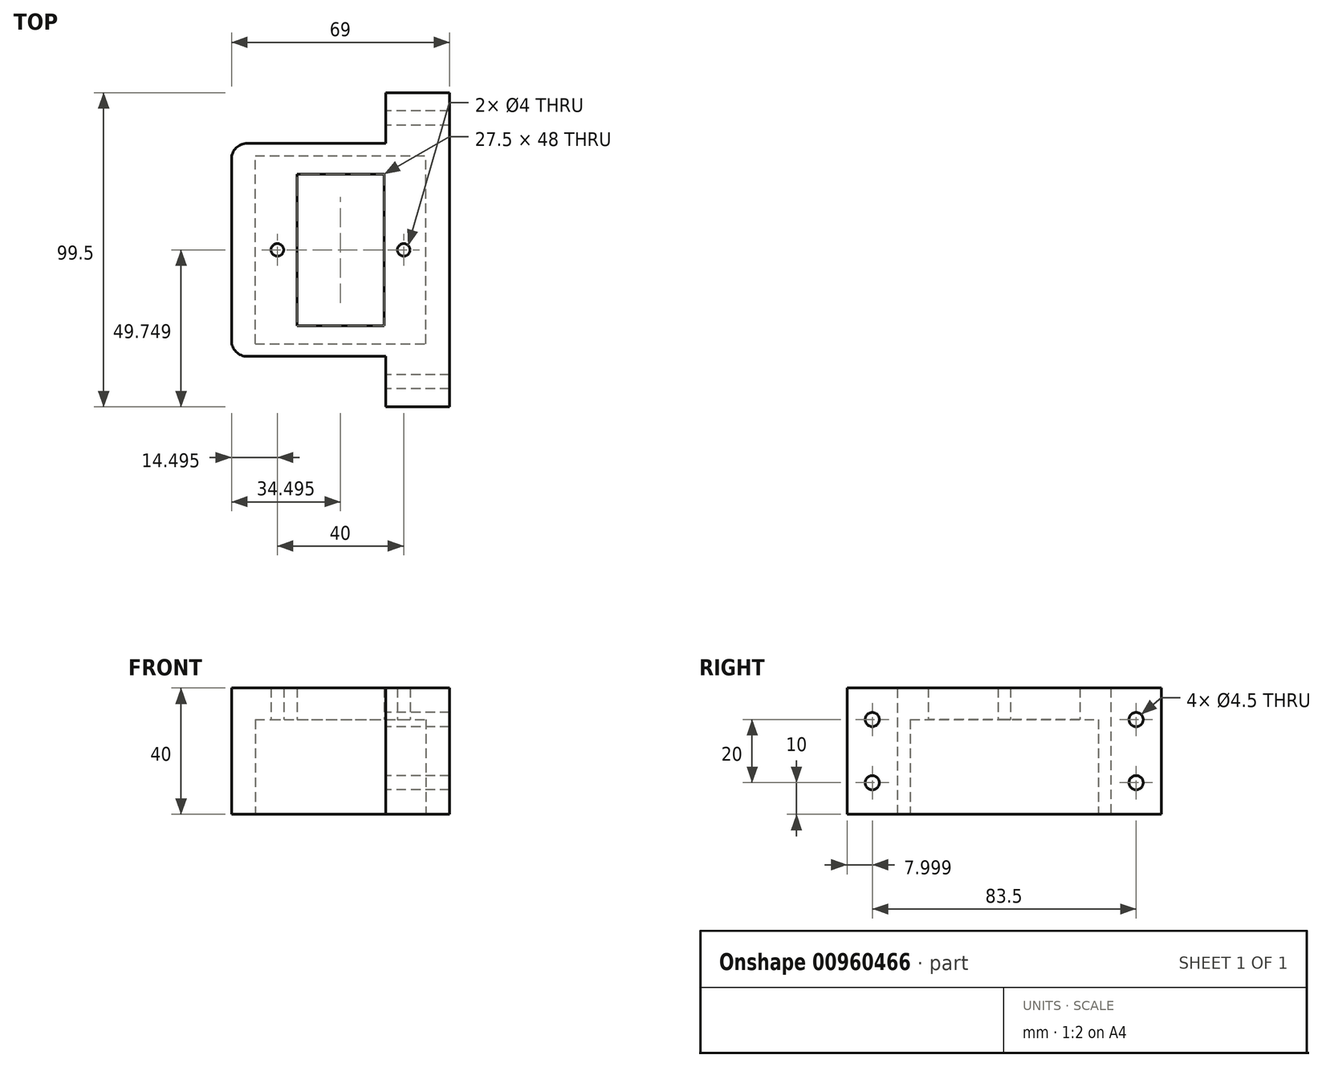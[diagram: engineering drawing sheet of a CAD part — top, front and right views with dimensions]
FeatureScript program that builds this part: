
annotation { "Feature Type Name" : "Feature", "Feature Type Description" : "" }
export const myFeature = defineFeature(function(context is Context, id is Id, definition is map)
    precondition{}
    {
        {
            var Q0;
            Q0=qCreatedBy(makeId("Top.planeOp"),FACE);
            var sketch = newSketch(context, id + "F0", { "sketchPlane" : qUnion([Q0])});
            skLineSegment(sketch, "E0.bottom", {"start": v(-20.47, 12.83) * mm, "end": v(7.03, 12.83) * mm});
            skLineSegment(sketch, "E0.top", {"start": v(-20.47, -35.17) * mm, "end": v(7.03, -35.17) * mm});
            skLineSegment(sketch, "E0.left", {"start": v(-20.47, 12.83) * mm, "end": v(-20.47, -35.17) * mm});
            skLineSegment(sketch, "E0.right", {"start": v(7.03, 12.83) * mm, "end": v(7.03, -35.17) * mm});
            skLineSegment(sketch, "E1", {"start": v(-20.47, -11.17) * mm, "end": v(-98.82, -11.17) * mm, "construction": true});
            skLineSegment(sketch, "E2", {"start": v(7.03, -11.17) * mm, "end": v(89.84, -11.17) * mm, "construction": true});
            skCircle(sketch, "E3", {"center": v(-26.72, -11.17) * mm, "radius": 2 * mm});
            skCircle(sketch, "E4", {"center": v(13.28, -11.17) * mm, "radius": 2 * mm});
            skLineSegment(sketch, "E5", {"start": v(-6.72, -35.17) * mm, "end": v(-6.72, 12.83) * mm, "construction": true});
            skLineSegment(sketch, "E6.bottom", {"start": v(-41.22, 38.58) * mm, "end": v(27.78, 38.58) * mm});
            skLineSegment(sketch, "E6.top", {"start": v(-41.22, -60.92) * mm, "end": v(27.78, -60.92) * mm});
            skLineSegment(sketch, "E6.left", {"start": v(-41.22, 38.58) * mm, "end": v(-41.22, -60.92) * mm});
            skLineSegment(sketch, "E6.right", {"start": v(27.78, 38.58) * mm, "end": v(27.78, -60.92) * mm});
            skLineSegment(sketch, "E7", {"start": v(-21.02, 18.58) * mm, "end": v(7.58, 18.58) * mm});
            skLineSegment(sketch, "E8", {"start": v(-20.47, -11.17) * mm, "end": v(7.03, -11.17) * mm, "construction": true});
            skLineSegment(sketch, "E9", {"start": v(-21.02, -40.92) * mm, "end": v(7.58, -40.92) * mm});
            skPoint(sketch, "E10", {"position": v(-31.22, -11.17) * mm});
            skPoint(sketch, "E11", {"position": v(17.78, -11.17) * mm});
            skLineSegment(sketch, "E12", {"start": v(-31.22, -11.17) * mm, "end": v(-21.02, 18.58) * mm});
            skLineSegment(sketch, "E13", {"start": v(7.58, 18.58) * mm, "end": v(17.78, -11.17) * mm});
            skLineSegment(sketch, "E14", {"start": v(17.78, -11.17) * mm, "end": v(7.58, -40.92) * mm});
            skLineSegment(sketch, "E15", {"start": v(-21.02, -40.92) * mm, "end": v(-31.22, -11.17) * mm});
            skSolve(sketch);
        }
        {
            var Q0;
            Q0=makeQuery(id+"F0.imprint","IMPRINT",FACE,{"disambiguationData":[TD([[makeQuery(id+"F0.imprint","IMPRINT",EDGE,{"derivedFrom":sQuery(id+"F0.wireOp",EDGE,"E0.bottom")}),1.0]])]});
            extrude(context, id + "F1", {"entities" : qUnion([Q0]), "depth" : 1 * mm, "offsetDistance" : 25 * mm});
        }
        {
            var Q0;
            Q0=makeQuery(id+"F0.imprint","IMPRINT",FACE,{"disambiguationData":[TD([[makeQuery(id+"F0.imprint","IMPRINT",EDGE,{"derivedFrom":sQuery(id+"F0.wireOp",EDGE,"E6.bottom")}),-1.0]])]});
            var Q1;
            Q1=makeQuery(id+"F0.imprint","IMPRINT",FACE,{"disambiguationData":[TD([[makeQuery(id+"F0.imprint","IMPRINT",EDGE,{"derivedFrom":sQuery(id+"F0.wireOp",EDGE,"E0.bottom")}),1.0]])]});
            extrude(context, id + "F2", {"entities" : qUnion([Q0, Q1]), "operationType" : NewBodyOperationType.ADD, "oppositeDirection" : true, "depth" : 40 * mm, "offsetDistance" : 25 * mm});
        }
        {
            var Q0;
            Q0=makeQuery(id+"F2.opExtrude","CAP_FACE",FACE,{"disambiguationData":[OSD([sQuery(id+"F0.wireOp",EDGE,"E0.bottom"),sQuery(id+"F0.wireOp",EDGE,"E0.top"),sQuery(id+"F0.wireOp",EDGE,"E0.left"),sQuery(id+"F0.wireOp",EDGE,"E0.right"),sQuery(id+"F0.wireOp",EDGE,"E3"),sQuery(id+"F0.wireOp",EDGE,"E4"),sQuery(id+"F0.wireOp",EDGE,"E6.bottom"),sQuery(id+"F0.wireOp",EDGE,"E6.top"),sQuery(id+"F0.wireOp",EDGE,"E6.left"),sQuery(id+"F0.wireOp",EDGE,"E6.right")])],"isStart":false});
            var sketch = newSketch(context, id + "F3", { "sketchPlane" : qUnion([Q0])});
            skLineSegment(sketch, "E16.bottom", {"start": v(-33.72, 40.92) * mm, "end": v(20.28, 40.92) * mm});
            skLineSegment(sketch, "E16.top", {"start": v(-33.72, -18.58) * mm, "end": v(20.28, -18.58) * mm});
            skLineSegment(sketch, "E16.left", {"start": v(-33.72, 40.92) * mm, "end": v(-33.72, -18.58) * mm});
            skLineSegment(sketch, "E16.right", {"start": v(20.28, 40.92) * mm, "end": v(20.28, -18.58) * mm});
            skSolve(sketch);
        }
        {
            var Q0;
            Q0=makeQuery(id+"F3.imprint","IMPRINT",FACE,{"disambiguationData":[TD([[makeQuery(id+"F3.imprint","IMPRINT",EDGE,{"derivedFrom":sQuery(id+"F3.wireOp",EDGE,"E16.bottom")}),-1.0]])]});
            var Q1;
            Q1=makeQuery(id+"F3.imprint","IMPRINT",FACE,{"disambiguationData":[TD([[makeQuery(id+"F3.imprint","IMPRINT",EDGE,{"derivedFrom":makeQuery(id+"F2.opExtrude","CAP_EDGE",EDGE,{"disambiguationData":[OSD([sQuery(id+"F0.wireOp",EDGE,"E3")])],"isStart":false})}),-1.0]])]});
            var Q2;
            Q2=makeQuery(id+"F3.imprint","IMPRINT",FACE,{"disambiguationData":[TD([[makeQuery(id+"F3.imprint","IMPRINT",EDGE,{"derivedFrom":makeQuery(id+"F2.opExtrude","CAP_EDGE",EDGE,{"disambiguationData":[OSD([sQuery(id+"F0.wireOp",EDGE,"E4")])],"isStart":false})}),-1.0]])]});
            extrude(context, id + "F4", {"entities" : qUnion([Q0, Q1, Q2]), "operationType" : NewBodyOperationType.REMOVE, "oppositeDirection" : true, "depth" : 30 * mm, "offsetDistance" : 25 * mm});
        }
        {
            var Q0;
            Q0=makeQuery(id+"F2.opExtrude","CAP_FACE",FACE,{"disambiguationData":[OSD([sQuery(id+"F0.wireOp",EDGE,"E0.bottom"),sQuery(id+"F0.wireOp",EDGE,"E0.top"),sQuery(id+"F0.wireOp",EDGE,"E0.left"),sQuery(id+"F0.wireOp",EDGE,"E0.right"),sQuery(id+"F0.wireOp",EDGE,"E3"),sQuery(id+"F0.wireOp",EDGE,"E4"),sQuery(id+"F0.wireOp",EDGE,"E6.bottom"),sQuery(id+"F0.wireOp",EDGE,"E6.top"),sQuery(id+"F0.wireOp",EDGE,"E6.left"),sQuery(id+"F0.wireOp",EDGE,"E6.right")])],"isStart":true});
            var sketch = newSketch(context, id + "F5", { "sketchPlane" : qUnion([Q0])});
            skLineSegment(sketch, "E17", {"start": v(7.58, -40.92) * mm, "end": v(7.58, -60.92) * mm});
            skLineSegment(sketch, "E18", {"start": v(7.58, 18.58) * mm, "end": v(7.58, 38.58) * mm});
            skLineSegment(sketch, "E19.0", {"start": v(-33.72, 18.58) * mm, "end": v(20.28, 18.58) * mm, "construction": true});
            skLineSegment(sketch, "E19.1", {"start": v(-33.72, -40.92) * mm, "end": v(20.28, -40.92) * mm, "construction": true});
            skLineSegment(sketch, "E19.2", {"start": v(-33.72, -40.92) * mm, "end": v(-33.72, 18.58) * mm, "construction": true});
            skLineSegment(sketch, "E20", {"start": v(7.58, -44.92) * mm, "end": v(-41.22, -44.92) * mm});
            skLineSegment(sketch, "E21", {"start": v(7.58, 22.58) * mm, "end": v(-41.22, 22.58) * mm});
            skSolve(sketch);
        }
        {
            var Q0;
            {var subQ3=sQuery(id+"F5.wireOp",EDGE,"E20");Q0=makeQuery(id+"F5.imprint","IMPRINT",FACE,{"disambiguationData":[TD([[makeQuery(id+"F5.imprint","IMPRINT",EDGE,{"derivedFrom":subQ3}),1.0]])]});}
            var Q1;
            {var subQ3=sQuery(id+"F5.wireOp",EDGE,"E21");Q1=makeQuery(id+"F5.imprint","IMPRINT",FACE,{"disambiguationData":[TD([[makeQuery(id+"F5.imprint","IMPRINT",EDGE,{"derivedFrom":subQ3}),-1.0]])]});}
            extrude(context, id + "F6", {"entities" : qUnion([Q0, Q1]), "operationType" : NewBodyOperationType.REMOVE, "endBound" : BoundingType.THROUGH_ALL, "oppositeDirection" : true, "depth" : 35 * mm, "offsetDistance" : 25 * mm});
        }
        {
            var Q0;
            Q0=makeQuery(id+"F6.boolean.opBoolean","COPY",FACE,{"derivedFrom":makeQuery(id+"F6.opExtrude","SWEPT_FACE",FACE,{"disambiguationData":[OSD([sQuery(id+"F5.wireOp",EDGE,"E17")])]})});
            var sketch = newSketch(context, id + "F7", { "sketchPlane" : qUnion([Q0])});
            skLineSegment(sketch, "E22.0.0", {"start": v(-22.58, 0) * mm, "end": v(-38.58, 0) * mm});
            skLineSegment(sketch, "E22.0.1", {"start": v(-38.58, 0) * mm, "end": v(-38.58, -35) * mm});
            skLineSegment(sketch, "E22.0.2", {"start": v(-38.58, -35) * mm, "end": v(-22.58, -35) * mm});
            skLineSegment(sketch, "E22.0.3", {"start": v(-22.58, -35) * mm, "end": v(-22.58, 0) * mm});
            skLineSegment(sketch, "E23", {"start": v(-30.58, 0) * mm, "end": v(-30.58, -35) * mm, "construction": true});
            skPoint(sketch, "E24", {"position": v(-30.58, -10) * mm});
            skPoint(sketch, "E25", {"position": v(-30.58, -30) * mm});
            skLineSegment(sketch, "E26.0", {"start": v(44.92, 0) * mm, "end": v(60.92, 0) * mm});
            skLineSegment(sketch, "E27.0", {"start": v(60.92, -35) * mm, "end": v(60.92, 0) * mm});
            skLineSegment(sketch, "E28.0", {"start": v(44.92, -35) * mm, "end": v(44.92, 0) * mm});
            skLineSegment(sketch, "E29", {"start": v(52.92, 0) * mm, "end": v(52.92, -35) * mm, "construction": true});
            skPoint(sketch, "E30", {"position": v(52.92, -10) * mm});
            skPoint(sketch, "E31", {"position": v(52.92, -30) * mm});
            skCircle(sketch, "E32", {"center": v(-30.58, -10) * mm, "radius": 2.25 * mm});
            skCircle(sketch, "E33", {"center": v(-30.58, -30) * mm, "radius": 2.25 * mm});
            skCircle(sketch, "E34", {"center": v(52.92, -10) * mm, "radius": 2.25 * mm});
            skCircle(sketch, "E35", {"center": v(52.92, -30) * mm, "radius": 2.25 * mm});
            skSolve(sketch);
        }
        {
            var Q0;
            Q0=makeQuery(id+"F7.imprint","IMPRINT",FACE,{"disambiguationData":[TD([[makeQuery(id+"F7.imprint","IMPRINT",EDGE,{"derivedFrom":sQuery(id+"F7.wireOp",EDGE,"E34")}),1.0]])]});
            var Q1;
            Q1=makeQuery(id+"F7.imprint","IMPRINT",FACE,{"disambiguationData":[TD([[makeQuery(id+"F7.imprint","IMPRINT",EDGE,{"derivedFrom":sQuery(id+"F7.wireOp",EDGE,"E35")}),1.0]])]});
            var Q2;
            Q2=makeQuery(id+"F7.imprint","IMPRINT",FACE,{"disambiguationData":[TD([[makeQuery(id+"F7.imprint","IMPRINT",EDGE,{"derivedFrom":sQuery(id+"F7.wireOp",EDGE,"E32")}),1.0]])]});
            var Q3;
            Q3=makeQuery(id+"F7.imprint","IMPRINT",FACE,{"disambiguationData":[TD([[makeQuery(id+"F7.imprint","IMPRINT",EDGE,{"derivedFrom":sQuery(id+"F7.wireOp",EDGE,"E33")}),1.0]])]});
            extrude(context, id + "F8", {"entities" : qUnion([Q0, Q1, Q2, Q3]), "operationType" : NewBodyOperationType.REMOVE, "endBound" : BoundingType.THROUGH_ALL, "oppositeDirection" : true, "depth" : 25 * mm, "offsetDistance" : 25 * mm});
        }
        {
            var Q0;
            Q0=makeQuery(id+"F1.opExtrude","CAP_FACE",FACE,{"disambiguationData":[OSD([sQuery(id+"F0.wireOp",EDGE,"E0.bottom"),sQuery(id+"F0.wireOp",EDGE,"E0.top"),sQuery(id+"F0.wireOp",EDGE,"E0.left"),sQuery(id+"F0.wireOp",EDGE,"E0.right"),sQuery(id+"F0.wireOp",EDGE,"E3"),sQuery(id+"F0.wireOp",EDGE,"E4"),sQuery(id+"F0.wireOp",EDGE,"E7"),sQuery(id+"F0.wireOp",EDGE,"E9"),sQuery(id+"F0.wireOp",EDGE,"E12"),sQuery(id+"F0.wireOp",EDGE,"E13"),sQuery(id+"F0.wireOp",EDGE,"E14"),sQuery(id+"F0.wireOp",EDGE,"E15")])],"isStart":false});
            extrude(context, id + "F9", {"entities" : qUnion([Q0]), "operationType" : NewBodyOperationType.REMOVE, "oppositeDirection" : true, "depth" : 1 * mm, "offsetDistance" : 25 * mm});
        }
        {
            var Q0;
            Q0=makeQuery(id+"F2.opExtrude","CAP_FACE",FACE,{"disambiguationData":[OSD([sQuery(id+"F0.wireOp",EDGE,"E0.bottom"),sQuery(id+"F0.wireOp",EDGE,"E0.top"),sQuery(id+"F0.wireOp",EDGE,"E0.left"),sQuery(id+"F0.wireOp",EDGE,"E0.right"),sQuery(id+"F0.wireOp",EDGE,"E3"),sQuery(id+"F0.wireOp",EDGE,"E4"),sQuery(id+"F0.wireOp",EDGE,"E6.bottom"),sQuery(id+"F0.wireOp",EDGE,"E6.top"),sQuery(id+"F0.wireOp",EDGE,"E6.left"),sQuery(id+"F0.wireOp",EDGE,"E6.right")])],"isStart":false});
            var sketch = newSketch(context, id + "F10", { "sketchPlane" : qUnion([Q0])});
            skLineSegment(sketch, "E36.0", {"start": v(7.58, 44.92) * mm, "end": v(-36.22, 44.92) * mm});
            skLineSegment(sketch, "E36.1", {"start": v(-41.22, -17.58) * mm, "end": v(-41.22, 39.92) * mm});
            skLineSegment(sketch, "E36.2", {"start": v(7.58, -22.58) * mm, "end": v(-36.22, -22.58) * mm});
            skPoint(sketch, "E37.visualSharp", {"position": v(-41.22, 44.92) * mm});
            skArc(sketch, "E37.filletArc", {"start": v(-36.22, 44.92) * mm, "mid": v(-39.76, 43.46) * mm, "end": v(-41.22, 39.92) * mm});
            skPoint(sketch, "E38.visualSharp", {"position": v(-41.22, -22.58) * mm});
            skArc(sketch, "E38.filletArc", {"start": v(-41.22, -17.58) * mm, "mid": v(-39.76, -21.11) * mm, "end": v(-36.22, -22.58) * mm});
            skLineSegment(sketch, "E39.0", {"start": v(-33.72, 40.92) * mm, "end": v(20.28, 40.92) * mm});
            skLineSegment(sketch, "E39.1", {"start": v(-33.72, 40.92) * mm, "end": v(-33.72, -18.58) * mm});
            skLineSegment(sketch, "E39.2", {"start": v(-33.72, -18.58) * mm, "end": v(20.28, -18.58) * mm});
            skLineSegment(sketch, "E39.3", {"start": v(20.28, 40.92) * mm, "end": v(20.28, -18.58) * mm});
            skSolve(sketch);
        }
        {
            var Q0;
            {var subQ0=sQuery(id+"F10.wireOp",EDGE,"E37.filletArc");Q0=makeQuery(id+"F10.imprint","IMPRINT",FACE,{"disambiguationData":[TD([[makeQuery(id+"F10.imprint","IMPRINT",EDGE,{"derivedFrom":subQ0}),-1.0]])]});}
            var Q1;
            {var subQ0=sQuery(id+"F10.wireOp",EDGE,"E38.filletArc");Q1=makeQuery(id+"F10.imprint","IMPRINT",FACE,{"disambiguationData":[TD([[makeQuery(id+"F10.imprint","IMPRINT",EDGE,{"derivedFrom":subQ0}),-1.0]])]});}
            extrude(context, id + "F11", {"entities" : qUnion([Q0, Q1]), "operationType" : NewBodyOperationType.REMOVE, "endBound" : BoundingType.THROUGH_ALL, "oppositeDirection" : true, "depth" : 25 * mm, "offsetDistance" : 25 * mm});
        }
    });
